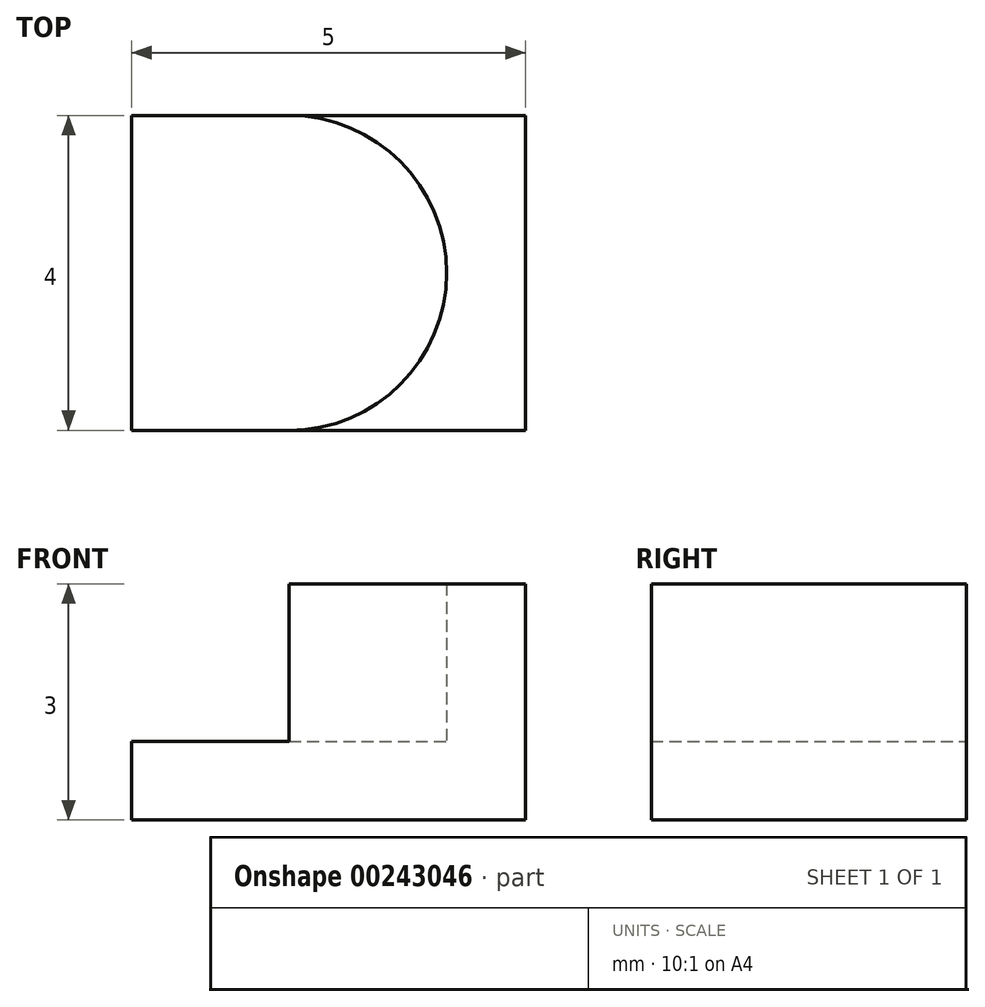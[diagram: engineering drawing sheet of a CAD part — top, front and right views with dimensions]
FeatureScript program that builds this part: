
annotation { "Feature Type Name" : "Feature", "Feature Type Description" : "" }
export const myFeature = defineFeature(function(context is Context, id is Id, definition is map)
    precondition{}
    {
        {
            var Q0;
            Q0=qCreatedBy(makeId("Top.planeOp"),FACE);
            var sketch = newSketch(context, id + "F0", { "sketchPlane" : qUnion([Q0])});
            skLineSegment(sketch, "E0.bottom", {"start": v(0, 0) * mm, "end": v(5, 0) * mm});
            skLineSegment(sketch, "E0.top", {"start": v(0, 4) * mm, "end": v(5, 4) * mm});
            skLineSegment(sketch, "E0.left", {"start": v(0, 0) * mm, "end": v(0, 4) * mm});
            skLineSegment(sketch, "E0.right", {"start": v(5, 0) * mm, "end": v(5, 4) * mm});
            skSolve(sketch);
        }
        {
            var Q0;
            Q0 = qSketchRegion(id + "F0", true);
            extrude(context, id + "F1", {"entities" : qUnion([Q0]), "depth" : 1 * mm});
        }
        {
            var Q0;
            Q0=makeQuery(id+"F1.opExtrude","CAP_FACE",FACE,{"disambiguationData":[OSD([sQuery(id+"F0.wireOp",EDGE,"E0.bottom"),sQuery(id+"F0.wireOp",EDGE,"E0.top"),sQuery(id+"F0.wireOp",EDGE,"E0.left"),sQuery(id+"F0.wireOp",EDGE,"E0.right")])],"isStart":false});
            var sketch = newSketch(context, id + "F2", { "sketchPlane" : qUnion([Q0])});
            skLineSegment(sketch, "E1", {"start": v(0, 4) * mm, "end": v(2, 4) * mm, "construction": true});
            skLineSegment(sketch, "E2", {"start": v(2, 4) * mm, "end": v(2, 0) * mm, "construction": true});
            skPoint(sketch, "E2.endSnap0", {"position": v(2.5, 0) * mm});
            skArc(sketch, "E3", {"start": v(2, 4) * mm, "mid": v(4, 2) * mm, "end": v(2, 0) * mm});
            skSolve(sketch);
        }
        {
            var Q0;
            {var subQ0=sQuery(id+"F2.wireOp",EDGE,"E3");Q0=makeQuery(id+"F2.imprint","IMPRINT",FACE,{"disambiguationData":[TD([[makeQuery(id+"F2.imprint","IMPRINT",EDGE,{"derivedFrom":subQ0}),-1.0]])]});}
            extrude(context, id + "F3", {"entities" : qUnion([Q0]), "operationType" : NewBodyOperationType.ADD, "depth" : 2 * mm});
        }
    });
